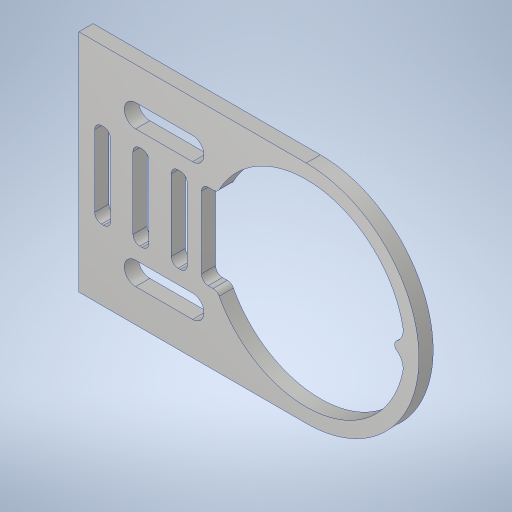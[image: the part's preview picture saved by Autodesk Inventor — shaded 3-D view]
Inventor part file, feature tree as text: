
AUTODESK INVENTOR PART (.ipt)
format: ipt  version: 2023.4 (Build 274418000, 418)  size: 355,328 bytes
history: native  units: in
note: dims shown in document units (in); Inventor stores cm internally (conversion verified against a paired STEP export)
features: extrude x4, sketch x4, fillet x2, projected_geometry x1
ambient origin geometry x8: Origin, YZ Plane, XZ Plane, XY Plane, X Axis, Y Axis, Z Axis, Center Point
bodies: Solid1 (feature_tree)
feature tree (11):
  extrude  "Extrusion1"  Depth=1.983in
  extrude  "Extrusion2"  Depth=0.125in
  extrude  "Extrusion3"  Depth=0.75in
  fillet  "Fillet1"  Radius=0.4901in
  extrude  "Extrusion4"  Depth=0.6151in
  fillet  "Fillet2"  Radius=0.125in
  sketch  "Sketch1"  dims[d0=2.0in d1=1.983in]
  sketch  "Sketch2"  dims[d3=0.125in d4=0.0in d6=0.125in]
  sketch  "Sketch3"  dims[d7=1.0in d8=0.75in d9=0.4901in]
  projected_geometry  "Projected Loop1"
  sketch  "Sketch4"  dims[d10=1.078in d11=0.6151in d12=0.125in d13=0.0in d14=0.0938in d15=0.825in d16=0.125in d17=0.0in d18=0.13in d19=0.125in d20=0.1969in d21=0.1969in d22=0.14in d23=0.14in d24=0.14in d25=0.75in d26=0.75in d27=0.75in d28=0.1393in d29=0.201in d30=0.201in d33=0.5in d34=0.5in d35=0.125in d36=0.125in d37=0.75in d38=1.0in d39=0.0in d40=0.06in]
